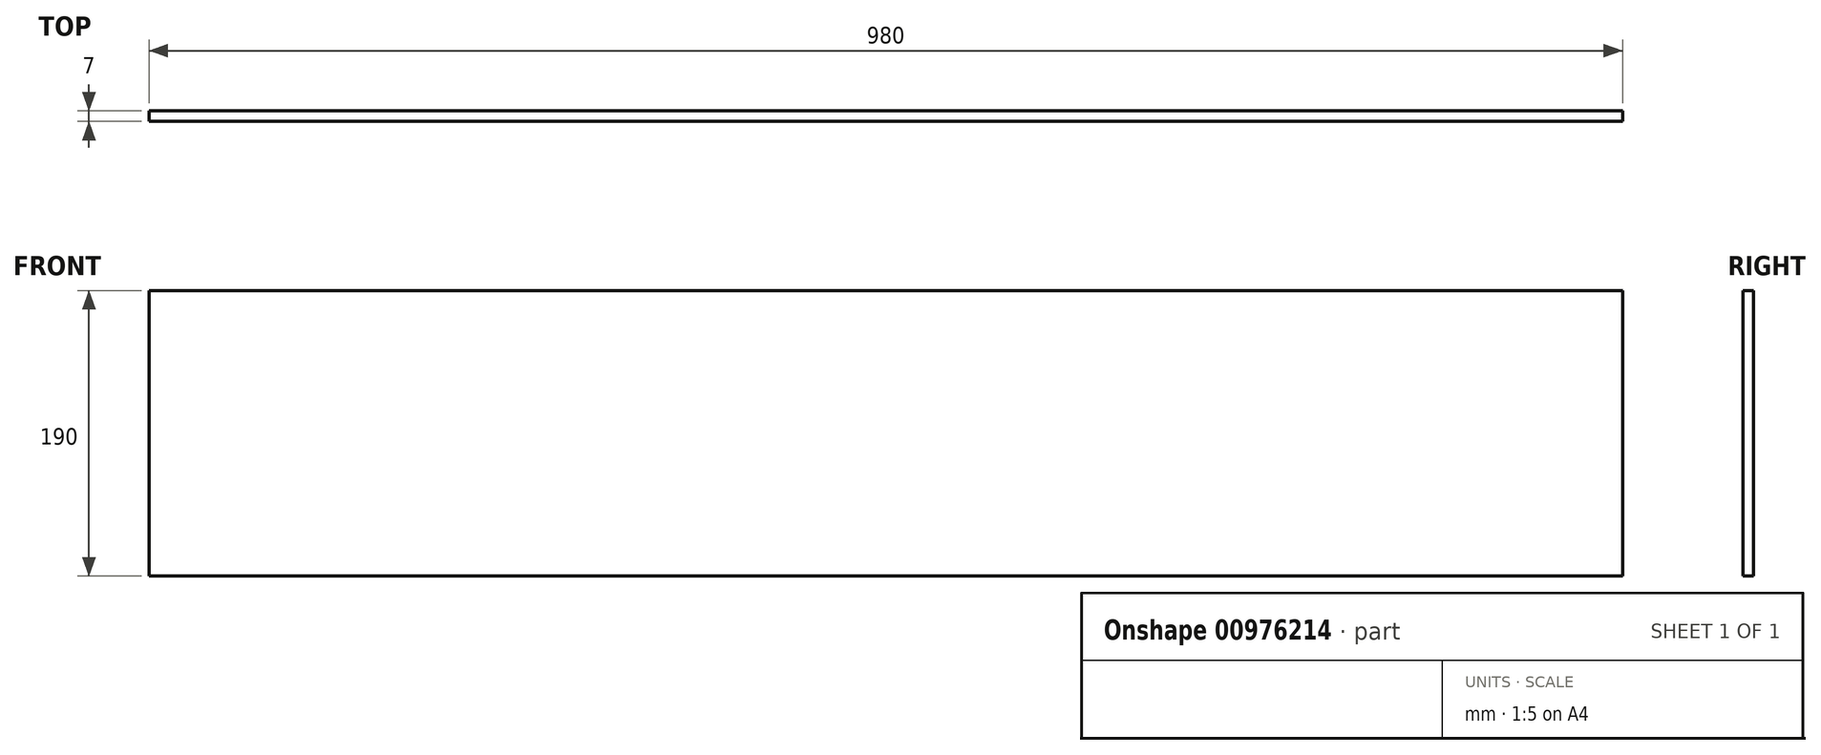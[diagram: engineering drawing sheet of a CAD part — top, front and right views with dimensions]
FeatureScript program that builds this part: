
annotation { "Feature Type Name" : "Feature", "Feature Type Description" : "" }
export const myFeature = defineFeature(function(context is Context, id is Id, definition is map)
    precondition{}
    {
        {
            var Q0;
            Q0=qCreatedBy(makeId("Front.planeOp"),FACE);
            var sketch = newSketch(context, id + "F0", { "sketchPlane" : qUnion([Q0])});
            skLineSegment(sketch, "E0.bottom", {"start": v(490, 95) * mm, "end": v(-490, 95) * mm});
            skLineSegment(sketch, "E0.top", {"start": v(490, -95) * mm, "end": v(-490, -95) * mm});
            skLineSegment(sketch, "E0.left", {"start": v(490, 95) * mm, "end": v(490, -95) * mm});
            skLineSegment(sketch, "E0.right", {"start": v(-490, 95) * mm, "end": v(-490, -95) * mm});
            skPoint(sketch, "E0.middle", {"position": v(0, 0) * mm});
            skSolve(sketch);
        }
        {
            var Q0;
            Q0=makeQuery(id+"F0.imprint","IMPRINT",FACE,{"disambiguationData":[TD([[makeQuery(id+"F0.imprint","IMPRINT",EDGE,{"derivedFrom":sQuery(id+"F0.wireOp",EDGE,"E0.bottom")}),1.0]])]});
            extrude(context, id + "F1", {"entities" : qUnion([Q0]), "depth" : 7 * mm, "offsetDistance" : 25 * mm});
        }
    });
